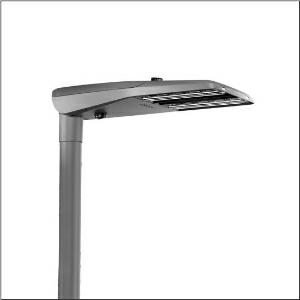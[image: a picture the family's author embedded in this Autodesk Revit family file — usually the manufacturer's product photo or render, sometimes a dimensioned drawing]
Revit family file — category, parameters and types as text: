
# Revit family: streetlight_sl_11_iq_midi___st1_0a_5xc3m51y08me_5fc7
name_source: partatom
category: Lighting Fixtures
units: mm (PartAtom-declared; Revit-internal decimal feet)

## family parameters
Cut with Voids When Loaded = No
Host = Face
Light Source = No
Part Type = Normal
Room Calculation Point = No
Round Connector Dimension = Use Diameter
Shared = No

## types (1)
- --- (1 x LED, 17540 lm, 122.7 W, 3000K)
    Apparent Load = 123 VA
    CIE Flux Codes = 33 66 96 100 100
    Color Rendering = 70
    Color Temperature = 3000K
    Default Elevation = 1800 mm
    Description = Streetlight SL 11 iQ midi, mast luminaire, primary light control with 3 zone facetted reflector, of plastic, silver coated, highly specular, primary optical cover: cover, of PMMA, transparent, light distribution: ST1.0a, light emission: direct distribution, primary light characteristic: asymmetric, installation type: post-top, side-entry, lamps: LED, High Power LED, rated values: 17.540lm | 122,7W | 143lm/W (begin service life); end service life: 17.540lm | 130,2W; at 50% lumin. flux: 8.770lm | 56,1W | 156,3lm/W, colour temperature: 3000K, colour rendering: CRI > 70, light colour: 730, light setting 1 begin service life: 100% | 17.540lm | 122,7W | 143lm/W | 3.000K, light setting 1 end service life: 130,2W, further light settings possible, control: pre-setting: logarithmic dimming characteristic, Street-Remote, Auto-Match, Temp-Guard, Lumen-Switch, Night-Set, Smart-Wire, Light-Fading, Desk-Remote (wireless, voltage-free reading and setting of iQ features in the workshop via application-optimized NFC function/RFID function), optimised constant luminous flux control (CLO 2.0), with cable H07RN-F 5x 1.5mm², mains connection: 230..240V, AC, 50/60Hz, connection cable pre-assembled, cable length: 12,5m, luminaire housing, of diecast aluminium, powder-coated, Siteco® metallic grey (DB 702S), please order mast flange separately, inclination adjustable without tools: 0°, 5°, 10°, 15° (post-top) | 0°, -5°, -10°, -15° (side-entry), sealing non-destructively replaceable, multi-level sealing system, length: 780mm, width: 376mm, height: 118mm, mast flange for spigot size: 42mm (side-entry): 5XC10008XM4, 60/48mm (side-entry/post-top): 5XC10108XM2, 76/60mm (side-entry/post-top): 5XC10108XM1, equipment: Power, Smart Interface below and above, protection rating (complete): IP66, insulation class (complete): insulation class II (safety insulation), certification: CE, ENEC, ENEC+, VDE, UKCA, impact resistance: IK10, permissible operating ambient temperature for outdoor applications: -25..+50°C, standard-compliant lighting for roads and squares, Environmental Product Declaration (EPD) tested and certified by an independent institute, packaging unit: 1 piece

Light Distribution: ST1.0a
    Height = 118 mm
    Lamp = 1 x LED
    Lamp Light Flux = 17540 lm
    Lamp Power = 122.7 W
    Lamp count = 1
    Length = 780 mm
    Luminous efficacy = 143 lm/W
    Manufacturer = Siteco
    ModVariant = No
    Model = 5XC3M51Y08ME
    Number of Poles = 1
    OnlyDefault = Yes
    Power Factor = 1
    Product Name = Streetlight SL 11 iQ midi | ST1.0a
    Product group = mast luminaire | pylon top
    ProductGroupID = 6100
    Protection Class = Protection class II
    Protection Degree = IP 66
    RLX_Detail_Level = 1
    RLX_Emergency_Light_Flux = 0 lm
    RLX_Emergency_Type = 0
    RLX_Emergency_Type_DB = No
    RlxData = <blob elided: 69357 chars, md5=593a41a3>
    Socket = socket
    Standby Power = 0 W
    System Light Flux = 17540 lm
    System Power = 123 W
    Type Comments = factory setting: luminous flux: 100 % | dim-lin: 254 | 553 mA
    Type Image = l_1004429.jpg
    URL = http://relux.com
    VarID = @adj_088414
    Voltage = 0 V
    Weight = 0.00 kg
    Width = 376 mm

## geometry (parser evidence)
native form markers: Blend x4, Sweep x11
no freeform markers — native parametric forms only
